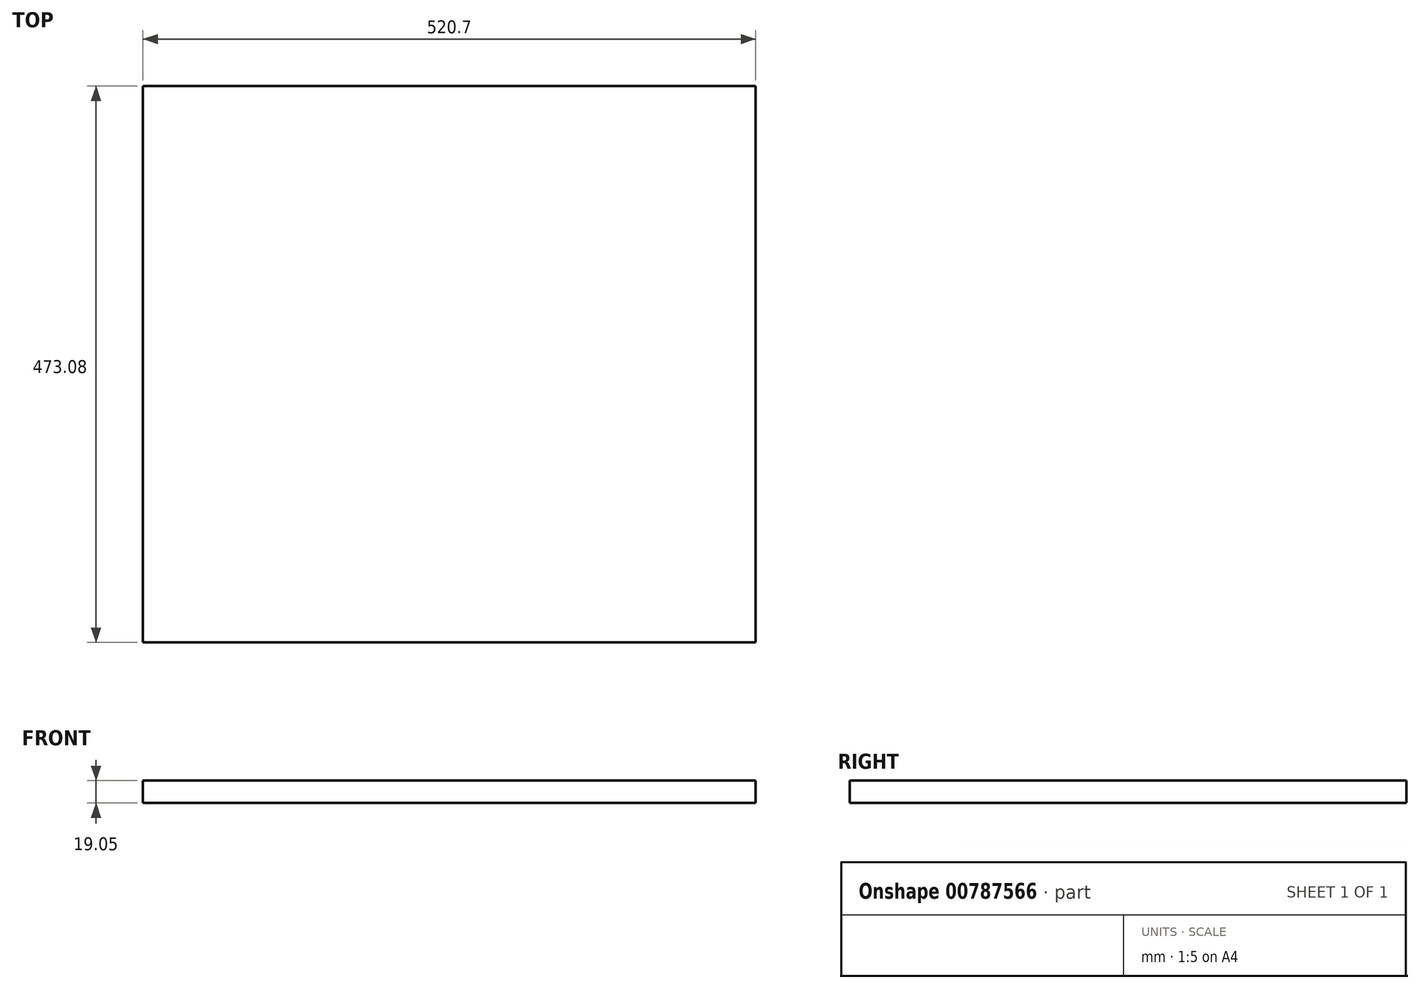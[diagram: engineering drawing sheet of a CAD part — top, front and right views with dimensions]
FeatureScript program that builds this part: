
annotation { "Feature Type Name" : "Feature", "Feature Type Description" : "" }
export const myFeature = defineFeature(function(context is Context, id is Id, definition is map)
    precondition{}
    {
        {
            var Q0;
            Q0=qCreatedBy(makeId("Top.planeOp"),FACE);
            var sketch = newSketch(context, id + "F0", { "sketchPlane" : qUnion([Q0])});
            skLineSegment(sketch, "E0.bottom", {"start": v(260.35, -236.54) * mm, "end": v(-260.35, -236.54) * mm});
            skLineSegment(sketch, "E0.top", {"start": v(260.35, 236.54) * mm, "end": v(-260.35, 236.54) * mm});
            skLineSegment(sketch, "E0.left", {"start": v(260.35, -236.54) * mm, "end": v(260.35, 236.54) * mm});
            skLineSegment(sketch, "E0.right", {"start": v(-260.35, -236.54) * mm, "end": v(-260.35, 236.54) * mm});
            skPoint(sketch, "E0.middle", {"position": v(0, 0) * mm});
            skSolve(sketch);
        }
        {
            var Q0;
            Q0 = qSketchRegion(id + "F0", true);
            var Q1;
            Q1=makeQuery(id+"F0.imprint","IMPRINT",FACE,{"disambiguationData":[TD([[makeQuery(id+"F0.imprint","IMPRINT",EDGE,{"derivedFrom":sQuery(id+"F0.wireOp",EDGE,"E0.bottom")}),-1.0]])]});
            extrude(context, id + "F1", {"entities" : qUnion([Q0, Q1]), "depth" : 19.05 * mm, "offsetDistance" : 25.4 * mm});
        }
    });
